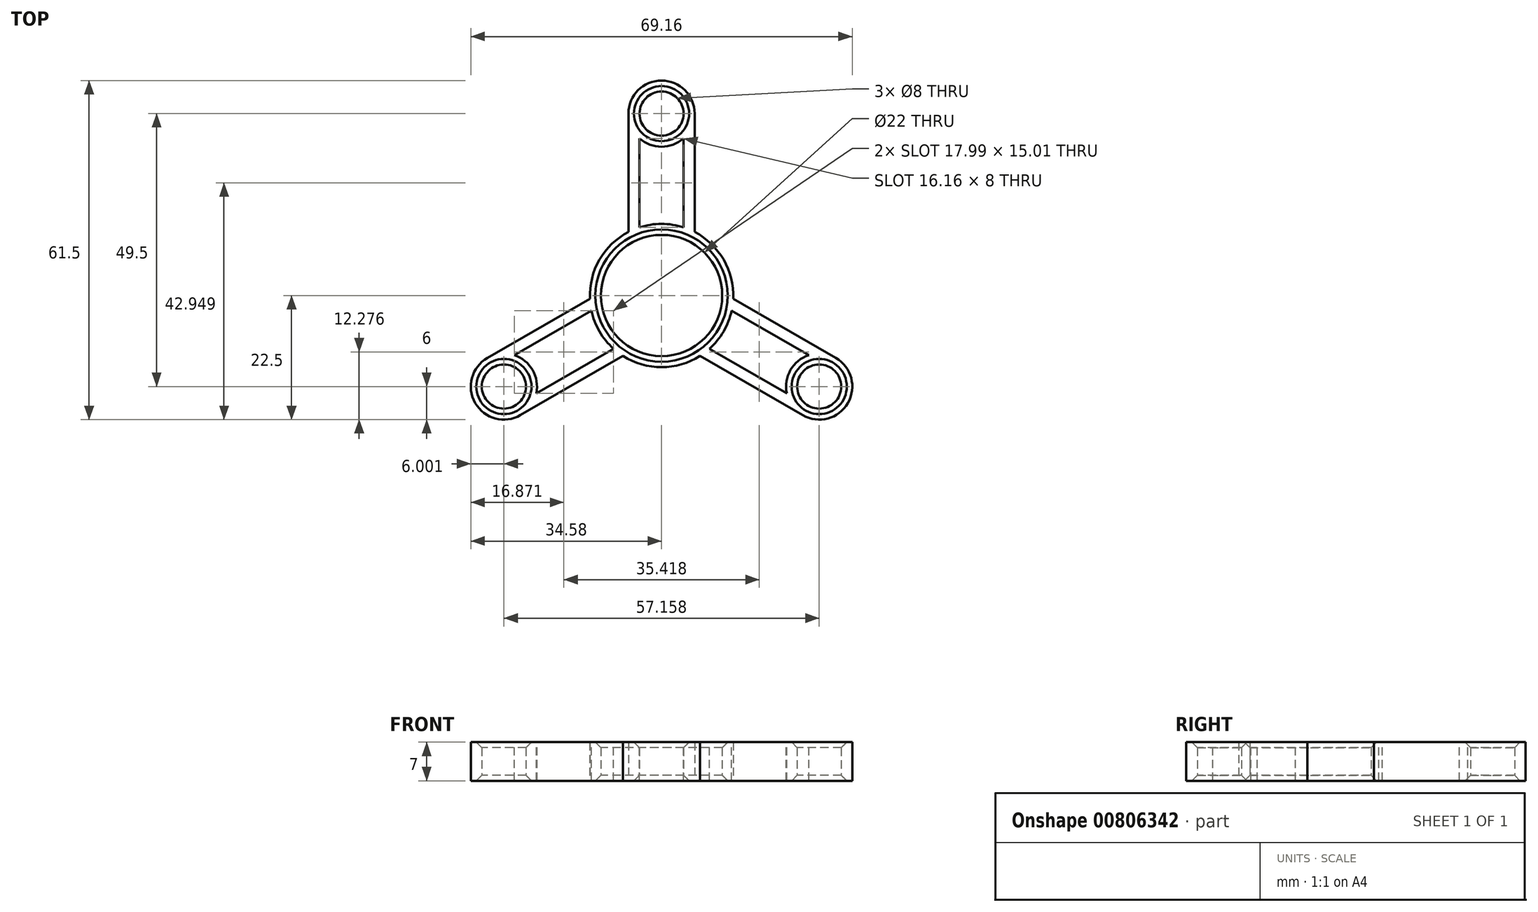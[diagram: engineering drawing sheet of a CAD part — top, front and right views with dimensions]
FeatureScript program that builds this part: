
annotation { "Feature Type Name" : "Feature", "Feature Type Description" : "" }
export const myFeature = defineFeature(function(context is Context, id is Id, definition is map)
    precondition{}
    {
        {
            var Q0;
            Q0=qCreatedBy(makeId("Top.planeOp"),FACE);
            var sketch = newSketch(context, id + "F0", { "sketchPlane" : qUnion([Q0])});
            skCircle(sketch, "E0", {"center": v(0, 0) * mm, "radius": 11 * mm});
            skCircle(sketch, "E1", {"center": v(0, 0) * mm, "radius": 13 * mm});
            skCircle(sketch, "E2", {"center": v(0, 33) * mm, "radius": 4 * mm});
            skCircle(sketch, "E3", {"center": v(0, 33) * mm, "radius": 6 * mm});
            skPoint(sketch, "E4.center", {"position": v(0, 0.5) * mm});
            skCircle(sketch, "E5.1.0", {"center": v(-28.58, -16.5) * mm, "radius": 6 * mm});
            skCircle(sketch, "E5.1.1", {"center": v(-28.58, -16.5) * mm, "radius": 4 * mm});
            skCircle(sketch, "E5.2.0", {"center": v(28.58, -16.5) * mm, "radius": 6 * mm});
            skCircle(sketch, "E5.2.1", {"center": v(28.58, -16.5) * mm, "radius": 4 * mm});
            skLineSegment(sketch, "E6", {"start": v(-6, 33) * mm, "end": v(-6, 11.53) * mm});
            skLineSegment(sketch, "E7", {"start": v(6, 33) * mm, "end": v(6, 11.53) * mm});
            skLineSegment(sketch, "E8.1.0", {"start": v(-25.58, -21.7) * mm, "end": v(-6.99, -10.96) * mm});
            skLineSegment(sketch, "E8.1.1", {"start": v(-31.58, -11.3) * mm, "end": v(-12.99, -0.57) * mm});
            skLineSegment(sketch, "E8.2.0", {"start": v(31.58, -11.3) * mm, "end": v(12.99, -0.57) * mm});
            skLineSegment(sketch, "E8.2.1", {"start": v(25.58, -21.7) * mm, "end": v(6.99, -10.96) * mm});
            skSolve(sketch);
        }
        {
            var Q0;
            Q0=makeQuery(id+"F0.imprint","IMPRINT",FACE,{"disambiguationData":[TD([[makeQuery(id+"F0.imprint","IMPRINT",EDGE,{"derivedFrom":sQuery(id+"F0.wireOp",EDGE,"E1")}),-1.0]])]});
            var Q1;
            Q1=makeQuery(id+"F0.imprint","IMPRINT",FACE,{"disambiguationData":[TD([[makeQuery(id+"F0.imprint","IMPRINT",EDGE,{"derivedFrom":sQuery(id+"F0.wireOp",EDGE,"c202e4ac-ae93-4b29-baa2-4fd0cf997ff0.1.0")}),-1.0]])]});
            var Q2;
            Q2=makeQuery(id+"F0.imprint","IMPRINT",FACE,{"disambiguationData":[TD([[makeQuery(id+"F0.imprint","IMPRINT",EDGE,{"derivedFrom":sQuery(id+"F0.wireOp",EDGE,"E0")}),-1.0]])]});
            var Q3;
            Q3=makeQuery(id+"F0.imprint","IMPRINT",FACE,{"disambiguationData":[TD([[makeQuery(id+"F0.imprint","IMPRINT",EDGE,{"derivedFrom":sQuery(id+"F0.wireOp",EDGE,"E2")}),-1.0]])]});
            var Q4;
            Q4=makeQuery(id+"F0.imprint","IMPRINT",FACE,{"disambiguationData":[TD([[makeQuery(id+"F0.imprint","IMPRINT",EDGE,{"derivedFrom":sQuery(id+"F0.wireOp",EDGE,"c202e4ac-ae93-4b29-baa2-4fd0cf997ff0.2.0")}),-1.0]])]});
            var Q5;
            Q5=makeQuery(id+"F0.imprint","IMPRINT",FACE,{"disambiguationData":[TD([[makeQuery(id+"F0.imprint","IMPRINT",EDGE,{"derivedFrom":sQuery(id+"F0.wireOp",EDGE,"0e0c9052-6751-44d5-bc73-aae295e7aca2.2.0")}),-1.0]])]});
            var Q6;
            Q6=makeQuery(id+"F0.imprint","IMPRINT",FACE,{"disambiguationData":[TD([[makeQuery(id+"F0.imprint","IMPRINT",EDGE,{"derivedFrom":sQuery(id+"F0.wireOp",EDGE,"0e0c9052-6751-44d5-bc73-aae295e7aca2.4.0")}),-1.0]])]});
            var Q7;
            Q7=makeQuery(id+"F0.imprint","IMPRINT",FACE,{"disambiguationData":[TD([[makeQuery(id+"F0.imprint","IMPRINT",EDGE,{"derivedFrom":sQuery(id+"F0.wireOp",EDGE,"6d77e2d1-ec52-477d-ae8a-bde1fbb15b47.4.1")}),-1.0]])]});
            var Q8;
            Q8=makeQuery(id+"F0.imprint","IMPRINT",FACE,{"disambiguationData":[TD([[makeQuery(id+"F0.imprint","IMPRINT",EDGE,{"derivedFrom":sQuery(id+"F0.wireOp",EDGE,"6d77e2d1-ec52-477d-ae8a-bde1fbb15b47.2.1")}),-1.0]])]});
            var Q9;
            Q9=makeQuery(id+"F0.imprint","IMPRINT",FACE,{"disambiguationData":[TD([[makeQuery(id+"F0.imprint","IMPRINT",EDGE,{"derivedFrom":sQuery(id+"F0.wireOp",EDGE,"3cc0715d-66bc-4789-9b96-2980e166defb.4.1")}),-1.0]])]});
            var Q10;
            Q10=makeQuery(id+"F0.imprint","IMPRINT",FACE,{"disambiguationData":[TD([[makeQuery(id+"F0.imprint","IMPRINT",EDGE,{"derivedFrom":sQuery(id+"F0.wireOp",EDGE,"3cc0715d-66bc-4789-9b96-2980e166defb.2.1")}),-1.0]])]});
            var Q11;
            Q11=makeQuery(id+"F0.imprint","IMPRINT",FACE,{"disambiguationData":[TD([[makeQuery(id+"F0.imprint","IMPRINT",EDGE,{"derivedFrom":sQuery(id+"F0.wireOp",EDGE,"E5.1.1")}),-1.0]])]});
            var Q12;
            Q12=makeQuery(id+"F0.imprint","IMPRINT",FACE,{"disambiguationData":[TD([[makeQuery(id+"F0.imprint","IMPRINT",EDGE,{"derivedFrom":sQuery(id+"F0.wireOp",EDGE,"E5.2.1")}),-1.0]])]});
            extrude(context, id + "F1", {"entities" : qUnion([Q0, Q1, Q2, Q3, Q4, Q5, Q6, Q7, Q8, Q9, Q10, Q11, Q12]), "endBound" : BoundingType.SYMMETRIC, "depth" : 7 * mm, "offsetDistance" : 25.4 * mm});
        }
        {
            var Q0;
            Q0=makeQuery(id+"F1.opExtrude","CAP_EDGE",EDGE,{"disambiguationData":[OSD([sQuery(id+"F0.wireOp",EDGE,"E2")])],"isStart":false});
            var Q1;
            Q1=makeQuery(id+"F1.opExtrude","CAP_EDGE",EDGE,{"disambiguationData":[OSD([sQuery(id+"F0.wireOp",EDGE,"E0")])],"isStart":false});
            var Q2;
            Q2=makeQuery(id+"F1.opExtrude","CAP_EDGE",EDGE,{"disambiguationData":[OSD([sQuery(id+"F0.wireOp",EDGE,"E5.1.1")])],"isStart":false});
            var Q3;
            Q3=makeQuery(id+"F1.opExtrude","CAP_EDGE",EDGE,{"disambiguationData":[OSD([sQuery(id+"F0.wireOp",EDGE,"E5.2.1")])],"isStart":false});
            var Q4;
            Q4=makeQuery(id+"F1.opExtrude","CAP_EDGE",EDGE,{"disambiguationData":[OSD([sQuery(id+"F0.wireOp",EDGE,"E5.1.1")])],"isStart":true});
            var Q5;
            Q5=makeQuery(id+"F1.opExtrude","CAP_EDGE",EDGE,{"disambiguationData":[OSD([sQuery(id+"F0.wireOp",EDGE,"E0")])],"isStart":true});
            var Q6;
            Q6=makeQuery(id+"F1.opExtrude","CAP_EDGE",EDGE,{"disambiguationData":[OSD([sQuery(id+"F0.wireOp",EDGE,"E5.2.1")])],"isStart":true});
            var Q7;
            Q7=makeQuery(id+"F1.opExtrude","CAP_EDGE",EDGE,{"disambiguationData":[OSD([sQuery(id+"F0.wireOp",EDGE,"E2")])],"isStart":true});
            chamfer(context, id + "F2", {"entities" : qUnion([Q0, Q1, Q2, Q3, Q4, Q5, Q6, Q7]), "width" : 1 * mm, "tangentPropagation" : true});
        }
        {
            var Q0;
            Q0=makeQuery(id+"F1.opExtrude","CAP_FACE",FACE,{"disambiguationData":[OSD([sQuery(id+"F0.wireOp",EDGE,"E0"),sQuery(id+"F0.wireOp",EDGE,"E1"),sQuery(id+"F0.wireOp",EDGE,"E2"),sQuery(id+"F0.wireOp",EDGE,"E3"),sQuery(id+"F0.wireOp",EDGE,"E5.1.0"),sQuery(id+"F0.wireOp",EDGE,"E5.1.1"),sQuery(id+"F0.wireOp",EDGE,"E5.2.0"),sQuery(id+"F0.wireOp",EDGE,"E5.2.1"),sQuery(id+"F0.wireOp",EDGE,"E6"),sQuery(id+"F0.wireOp",EDGE,"E7"),sQuery(id+"F0.wireOp",EDGE,"E8.1.0"),sQuery(id+"F0.wireOp",EDGE,"E8.1.1"),sQuery(id+"F0.wireOp",EDGE,"E8.2.0"),sQuery(id+"F0.wireOp",EDGE,"E8.2.1")])],"isStart":false});
            var sketch = newSketch(context, id + "F3", { "sketchPlane" : qUnion([Q0])});
            skCircle(sketch, "E9.0", {"center": v(0, 33) * mm, "radius": 6 * mm});
            skCircle(sketch, "E10.0", {"center": v(0, 0) * mm, "radius": 13 * mm});
            skLineSegment(sketch, "E11", {"start": v(-4, 28.53) * mm, "end": v(-4, 12.37) * mm});
            skLineSegment(sketch, "E12", {"start": v(4, 28.53) * mm, "end": v(4, 12.37) * mm});
            skLineSegment(sketch, "E13.1.0", {"start": v(-22.7, -17.73) * mm, "end": v(-8.71, -9.65) * mm});
            skLineSegment(sketch, "E13.1.1", {"start": v(-26.7, -10.8) * mm, "end": v(-12.71, -2.72) * mm});
            skCircle(sketch, "E13.1.2", {"center": v(-28.58, -16.5) * mm, "radius": 6 * mm});
            skLineSegment(sketch, "E13.2.0", {"start": v(26.7, -10.8) * mm, "end": v(12.71, -2.72) * mm});
            skLineSegment(sketch, "E13.2.1", {"start": v(22.7, -17.73) * mm, "end": v(8.71, -9.65) * mm});
            skCircle(sketch, "E13.2.2", {"center": v(28.58, -16.5) * mm, "radius": 6 * mm});
            skSolve(sketch);
        }
        {
            var Q0;
            {var subQ0=sQuery(id+"F3.wireOp",EDGE,"E11");Q0=makeQuery(id+"F3.imprint","IMPRINT",FACE,{"disambiguationData":[TD([[makeQuery(id+"F3.imprint","IMPRINT",EDGE,{"derivedFrom":subQ0}),1.0]])]});}
            var Q1;
            {var subQ0=sQuery(id+"F3.wireOp",EDGE,"E13.1.0");Q1=makeQuery(id+"F3.imprint","IMPRINT",FACE,{"disambiguationData":[TD([[makeQuery(id+"F3.imprint","IMPRINT",EDGE,{"derivedFrom":subQ0}),1.0]])]});}
            var Q2;
            {var subQ0=sQuery(id+"F3.wireOp",EDGE,"E13.2.0");Q2=makeQuery(id+"F3.imprint","IMPRINT",FACE,{"disambiguationData":[TD([[makeQuery(id+"F3.imprint","IMPRINT",EDGE,{"derivedFrom":subQ0}),1.0]])]});}
            extrude(context, id + "F4", {"entities" : qUnion([Q0, Q1, Q2]), "operationType" : NewBodyOperationType.REMOVE, "endBound" : BoundingType.THROUGH_ALL, "oppositeDirection" : true, "depth" : 25 * mm, "offsetDistance" : 25 * mm});
        }
    });
